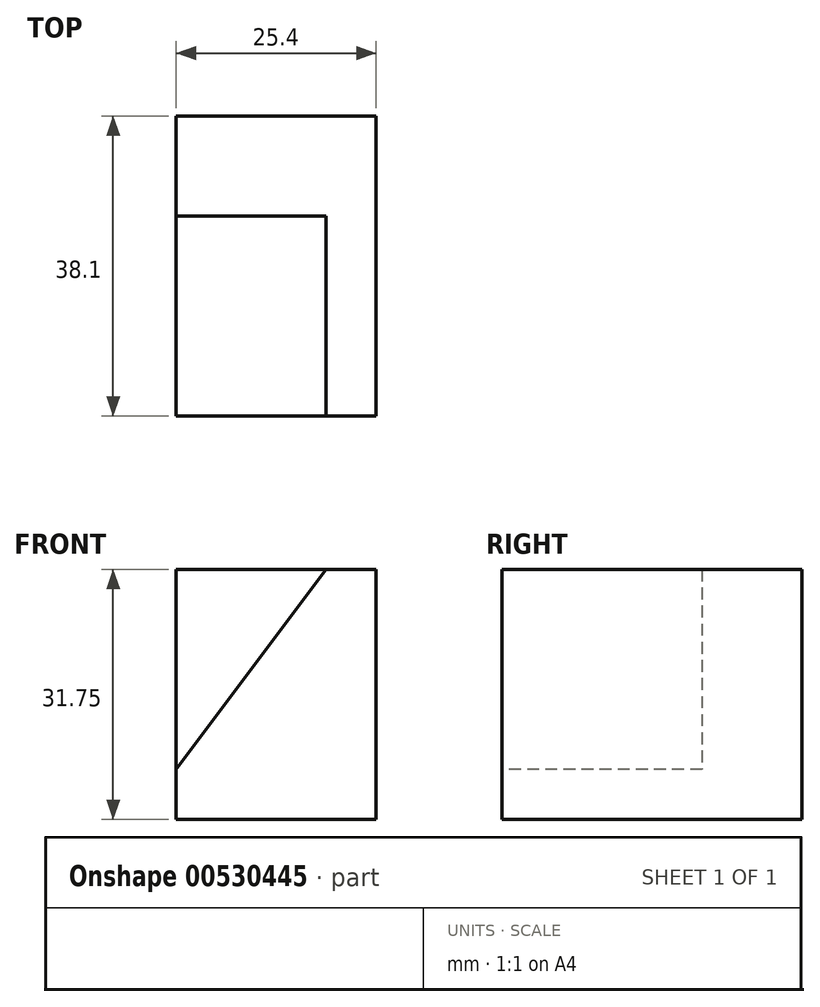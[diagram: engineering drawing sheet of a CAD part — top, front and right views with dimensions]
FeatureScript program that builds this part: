
annotation { "Feature Type Name" : "Feature", "Feature Type Description" : "" }
export const myFeature = defineFeature(function(context is Context, id is Id, definition is map)
    precondition{}
    {
        {
            var Q0;
            Q0=qCreatedBy(makeId("Front.planeOp"),FACE);
            var sketch = newSketch(context, id + "F0", { "sketchPlane" : qUnion([Q0])});
            skLineSegment(sketch, "E0", {"start": v(-13.81, 48.5) * mm, "end": v(-13.81, 16.75) * mm});
            skLineSegment(sketch, "E1", {"start": v(-13.81, 16.75) * mm, "end": v(-39.21, 16.75) * mm});
            skLineSegment(sketch, "E2", {"start": v(-39.21, 48.5) * mm, "end": v(-39.21, 16.75) * mm});
            skLineSegment(sketch, "E3", {"start": v(-39.21, 48.5) * mm, "end": v(-13.81, 48.5) * mm});
            skSolve(sketch);
        }
        {
            var Q0;
            Q0=makeQuery(id+"F0.imprint","IMPRINT",FACE,{"disambiguationData":[TD([[makeQuery(id+"F0.imprint","IMPRINT",EDGE,{"derivedFrom":sQuery(id+"F0.wireOp",EDGE,"E0")}),-1.0]])]});
            extrude(context, id + "F1", {"entities" : qUnion([Q0]), "depth" : 38.1 * mm, "offsetDistance" : 25.4 * mm});
        }
        {
            var Q0;
            Q0=makeQuery(id+"F1.opExtrude","CAP_FACE",FACE,{"disambiguationData":[OSD([sQuery(id+"F0.wireOp",EDGE,"E0"),sQuery(id+"F0.wireOp",EDGE,"E1"),sQuery(id+"F0.wireOp",EDGE,"E2"),sQuery(id+"F0.wireOp",EDGE,"E3")])],"isStart":false});
            var sketch = newSketch(context, id + "F2", { "sketchPlane" : qUnion([Q0])});
            skLineSegment(sketch, "E4", {"start": v(-20.16, 48.5) * mm, "end": v(-39.21, 23.1) * mm});
            skSolve(sketch);
        }
        {
            var Q0;
            {var subQ0=sQuery(id+"F2.wireOp",EDGE,"E4");Q0=makeQuery(id+"F2.imprint","IMPRINT",FACE,{"disambiguationData":[TD([[makeQuery(id+"F2.imprint","IMPRINT",EDGE,{"derivedFrom":subQ0}),-1.0]])]});}
            extrude(context, id + "F3", {"entities" : qUnion([Q0]), "operationType" : NewBodyOperationType.REMOVE, "oppositeDirection" : true, "depth" : 25.4 * mm, "offsetDistance" : 25.4 * mm});
        }
    });
